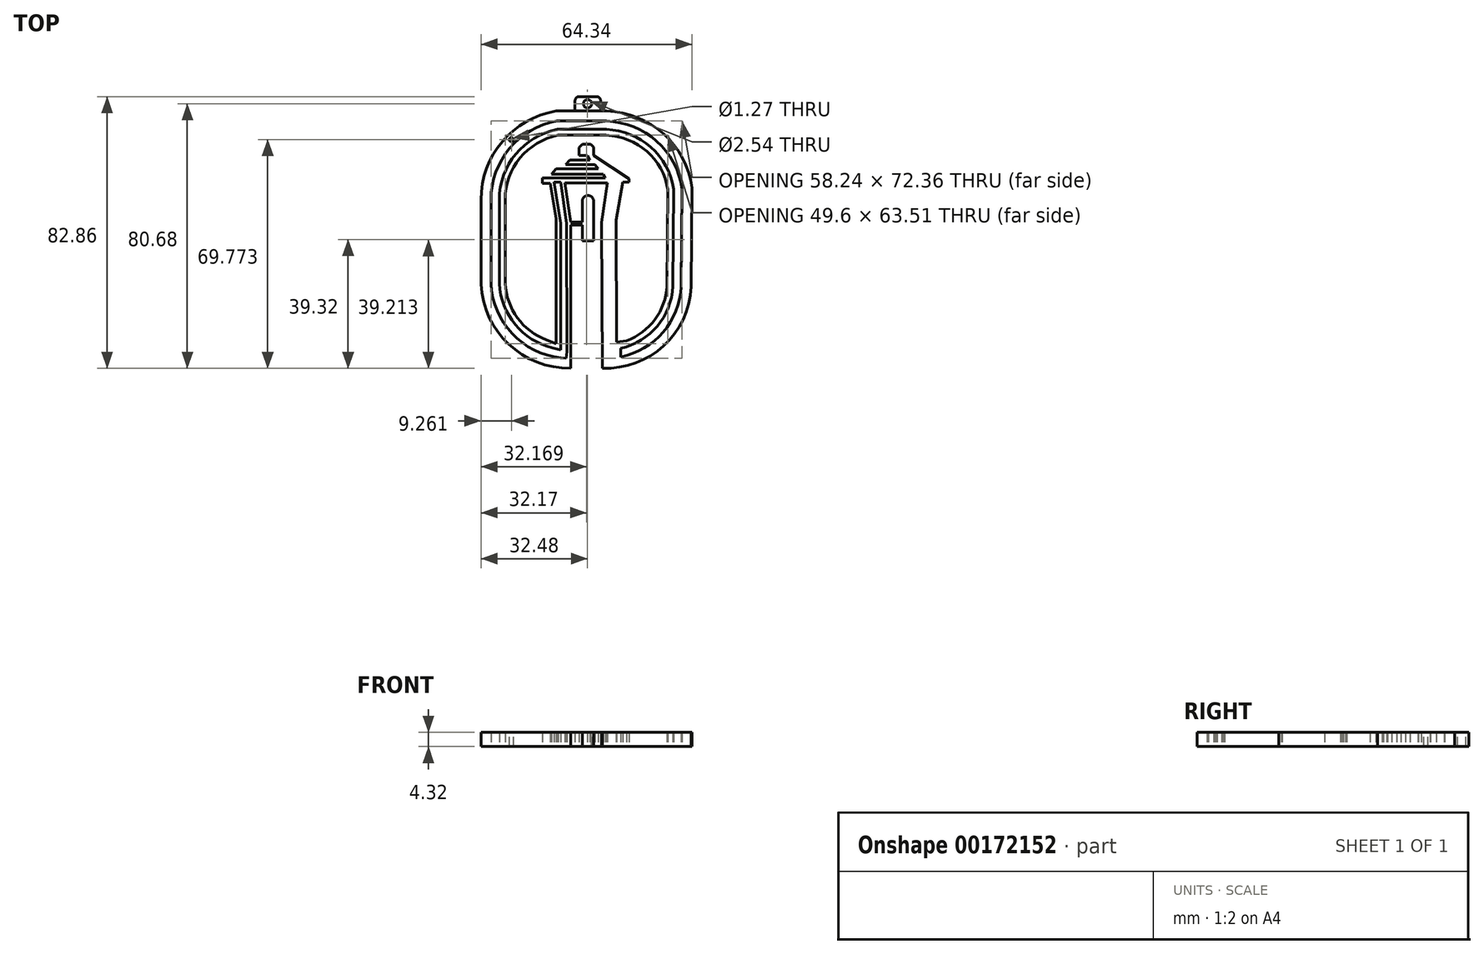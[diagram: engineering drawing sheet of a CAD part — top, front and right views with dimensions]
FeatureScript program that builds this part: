
annotation { "Feature Type Name" : "Feature", "Feature Type Description" : "" }
export const myFeature = defineFeature(function(context is Context, id is Id, definition is map)
    precondition{}
    {
        {
            var Q0;
            Q0=qCreatedBy(makeId("Top.planeOp"),FACE);
            var sketch = newSketch(context, id + "F0", { "sketchPlane" : qUnion([Q0])});
            skArc(sketch, "E0", {"start": v(-9.64, 42.68) * mm, "mid": v(-26, 33.33) * mm, "end": v(-32.48, 15.63) * mm});
            skArc(sketch, "E1", {"start": v(-32.48, -10.06) * mm, "mid": v(-24, -28.43) * mm, "end": v(-5.14, -35.74) * mm});
            skArc(sketch, "E2", {"start": v(4.52, -35.74) * mm, "mid": v(23.2, -28.91) * mm, "end": v(31.58, -10.89) * mm});
            skArc(sketch, "E3", {"start": v(31.86, 19.21) * mm, "mid": v(23.15, 35.73) * mm, "end": v(5.82, 42.68) * mm});
            skLineSegment(sketch, "E4", {"start": v(-9.64, 42.68) * mm, "end": v(5.82, 42.68) * mm});
            skLineSegment(sketch, "E5", {"start": v(-32.48, 15.63) * mm, "end": v(-32.48, -10.06) * mm});
            skLineSegment(sketch, "E6", {"start": v(31.58, -10.89) * mm, "end": v(31.86, 19.21) * mm});
            skLineSegment(sketch, "E7", {"start": v(-5.14, -35.74) * mm, "end": v(-5.14, 7.9) * mm});
            skLineSegment(sketch, "E8", {"start": v(-5.14, 8.72) * mm, "end": v(-6.88, 20.8) * mm});
            skLineSegment(sketch, "E9", {"start": v(-6.88, 20.8) * mm, "end": v(6.03, 20.8) * mm});
            skLineSegment(sketch, "E10", {"start": v(6.03, 20.8) * mm, "end": v(4.33, 8.72) * mm});
            skLineSegment(sketch, "E11", {"start": v(4.33, 8.72) * mm, "end": v(4.52, -35.74) * mm});
            skLineSegment(sketch, "E12.0", {"start": v(-9.37, 39.63) * mm, "end": v(5.78, 39.63) * mm});
            skLineSegment(sketch, "E12.1", {"start": v(-10.35, 23.5) * mm, "end": v(-10.4, 23.85) * mm});
            skLineSegment(sketch, "E12.2", {"start": v(-8.19, -30.15) * mm, "end": v(-8.19, 8.5) * mm});
            skArc(sketch, "E12.3", {"start": v(-29.43, -9.98) * mm, "mid": v(-22.96, -25.17) * mm, "end": v(-8.19, -32.55) * mm});
            skLineSegment(sketch, "E12.4", {"start": v(-29.43, 15.63) * mm, "end": v(-29.43, -9.98) * mm});
            skArc(sketch, "E12.6", {"start": v(-9.37, 39.63) * mm, "mid": v(-23.75, 31.27) * mm, "end": v(-29.43, 15.63) * mm});
            skArc(sketch, "E12.9", {"start": v(7.56, -32.63) * mm, "mid": v(22.16, -25.67) * mm, "end": v(28.54, -10.8) * mm});
            skLineSegment(sketch, "E12.10", {"start": v(28.54, -10.8) * mm, "end": v(28.8, 19.01) * mm});
            skArc(sketch, "E12.11", {"start": v(28.8, 19.01) * mm, "mid": v(21.05, 33.52) * mm, "end": v(5.78, 39.63) * mm});
            skArc(sketch, "E13.0", {"start": v(-9.14, 37.1) * mm, "mid": v(-21.88, 29.56) * mm, "end": v(-26.89, 15.63) * mm});
            skArc(sketch, "E13.4", {"start": v(-26.89, -9.92) * mm, "mid": v(-22.04, -22.38) * mm, "end": v(-10.73, -29.52) * mm});
            skLineSegment(sketch, "E13.6", {"start": v(-26.89, 15.63) * mm, "end": v(-26.89, -9.92) * mm});
            skArc(sketch, "E13.8", {"start": v(10.09, -29.68) * mm, "mid": v(21.24, -22.9) * mm, "end": v(26, -10.73) * mm});
            skLineSegment(sketch, "E13.9", {"start": v(26, -10.73) * mm, "end": v(26.27, 18.84) * mm});
            skArc(sketch, "E13.10", {"start": v(26.27, 18.84) * mm, "mid": v(19.3, 31.68) * mm, "end": v(5.74, 37.1) * mm});
            skLineSegment(sketch, "E13.11", {"start": v(-9.14, 37.1) * mm, "end": v(5.74, 37.1) * mm});
            skLineSegment(sketch, "E14.0", {"start": v(-8.97, 35.31) * mm, "end": v(5.7, 35.32) * mm});
            skArc(sketch, "E14.3", {"start": v(-25.1, -9.87) * mm, "mid": v(-21.36, -20.35) * mm, "end": v(-12.5, -27.1) * mm});
            skLineSegment(sketch, "E14.4", {"start": v(-25.1, 15.63) * mm, "end": v(-25.1, -9.87) * mm});
            skArc(sketch, "E14.6", {"start": v(-8.97, 35.31) * mm, "mid": v(-20.56, 28.36) * mm, "end": v(-25.1, 15.63) * mm});
            skArc(sketch, "E14.9", {"start": v(11.85, -27.32) * mm, "mid": v(20.56, -20.88) * mm, "end": v(24.22, -10.68) * mm});
            skLineSegment(sketch, "E14.10", {"start": v(24.22, -10.68) * mm, "end": v(24.49, 18.71) * mm});
            skArc(sketch, "E14.11", {"start": v(24.49, 18.71) * mm, "mid": v(18.08, 30.38) * mm, "end": v(5.7, 35.32) * mm});
            skLineSegment(sketch, "E15", {"start": v(1.88, 3.08) * mm, "end": v(1.88, 15.18) * mm});
            skArc(sketch, "E16", {"start": v(1.88, 15.18) * mm, "mid": v(0.12, 16.94) * mm, "end": v(-1.63, 15.18) * mm});
            skLineSegment(sketch, "E17", {"start": v(-1.63, 15.18) * mm, "end": v(-1.63, 8.8) * mm});
            skLineSegment(sketch, "E18", {"start": v(-1.63, 8.8) * mm, "end": v(-5.14, 8.8) * mm});
            skLineSegment(sketch, "E19", {"start": v(-5.14, 8.8) * mm, "end": v(-5.16, 8.84) * mm});
            skLineSegment(sketch, "E20", {"start": v(-5.14, 7.9) * mm, "end": v(-1.63, 7.9) * mm});
            skLineSegment(sketch, "E21", {"start": v(-1.63, 7.9) * mm, "end": v(-1.63, 3.08) * mm});
            skLineSegment(sketch, "E22", {"start": v(-1.63, 3.08) * mm, "end": v(1.88, 3.08) * mm});
            skLineSegment(sketch, "E23", {"start": v(-12.5, -27.1) * mm, "end": v(-9.61, -28.2) * mm});
            skLineSegment(sketch, "E24", {"start": v(-9.61, -28.2) * mm, "end": v(-9.61, 9.81) * mm});
            skLineSegment(sketch, "E25", {"start": v(-9.61, 9.81) * mm, "end": v(-11.31, 20.64) * mm});
            skLineSegment(sketch, "E26", {"start": v(-11.31, 20.64) * mm, "end": v(-13.8, 20.64) * mm});
            skLineSegment(sketch, "E27", {"start": v(-13.8, 20.64) * mm, "end": v(-13.8, 22.35) * mm});
            skLineSegment(sketch, "E28", {"start": v(-13.8, 22.35) * mm, "end": v(5.43, 22.35) * mm});
            skLineSegment(sketch, "E29", {"start": v(5.43, 22.35) * mm, "end": v(4.76, 23.5) * mm});
            skLineSegment(sketch, "E30", {"start": v(4.76, 23.5) * mm, "end": v(-11.01, 23.5) * mm});
            skLineSegment(sketch, "E31", {"start": v(-11.01, 23.5) * mm, "end": v(-9.58, 25.05) * mm});
            skLineSegment(sketch, "E32", {"start": v(-9.58, 25.05) * mm, "end": v(3.29, 25.05) * mm});
            skLineSegment(sketch, "E33", {"start": v(3.29, 25.05) * mm, "end": v(2.21, 26.4) * mm});
            skLineSegment(sketch, "E34", {"start": v(2.21, 26.4) * mm, "end": v(-6.65, 26.4) * mm});
            skLineSegment(sketch, "E35", {"start": v(-6.65, 26.4) * mm, "end": v(-5.42, 27.78) * mm});
            skLineSegment(sketch, "E36", {"start": v(-5.42, 27.78) * mm, "end": v(0.68, 27.78) * mm});
            skLineSegment(sketch, "E37", {"start": v(0.68, 27.78) * mm, "end": v(0, 29.2) * mm});
            skLineSegment(sketch, "E38", {"start": v(0, 29.2) * mm, "end": v(-2.64, 29.2) * mm});
            skLineSegment(sketch, "E39", {"start": v(-2.64, 29.2) * mm, "end": v(-2.64, 31.6) * mm});
            skLineSegment(sketch, "E40", {"start": v(-2.64, 31.6) * mm, "end": v(-1.54, 32.52) * mm});
            skLineSegment(sketch, "E41", {"start": v(-1.54, 32.52) * mm, "end": v(1, 32.52) * mm});
            skLineSegment(sketch, "E42", {"start": v(1, 32.52) * mm, "end": v(1.85, 31.66) * mm});
            skLineSegment(sketch, "E43", {"start": v(1.85, 31.66) * mm, "end": v(1.85, 29.2) * mm});
            skLineSegment(sketch, "E44", {"start": v(1.85, 29.2) * mm, "end": v(12.7, 22.05) * mm});
            skLineSegment(sketch, "E45", {"start": v(12.7, 22.05) * mm, "end": v(12.7, 20.99) * mm});
            skLineSegment(sketch, "E46", {"start": v(12.7, 20.99) * mm, "end": v(10.7, 20.99) * mm});
            skLineSegment(sketch, "E47", {"start": v(10.7, 20.99) * mm, "end": v(8.74, 9.5) * mm});
            skLineSegment(sketch, "E48", {"start": v(8.74, 9.5) * mm, "end": v(8.9, -27.8) * mm});
            skLineSegment(sketch, "E49", {"start": v(8.9, -27.8) * mm, "end": v(11.85, -27.32) * mm});
            skLineSegment(sketch, "E50", {"start": v(-10.73, -29.52) * mm, "end": v(-8.19, -30.15) * mm});
            skLineSegment(sketch, "E51", {"start": v(10.09, -29.68) * mm, "end": v(10.09, -32.27) * mm});
            skLineSegment(sketch, "E52", {"start": v(-8.19, 8.5) * mm, "end": v(-10.15, 21) * mm});
            skLineSegment(sketch, "E53", {"start": v(-10.15, 21) * mm, "end": v(-8.19, 21) * mm});
            skLineSegment(sketch, "E54", {"start": v(-8.19, 21) * mm, "end": v(-6.38, 8.5) * mm});
            skLineSegment(sketch, "E55", {"start": v(-6.38, 8.5) * mm, "end": v(-6.22, -30.63) * mm});
            skLineSegment(sketch, "E56", {"start": v(-8.19, -32.55) * mm, "end": v(-6.54, -32.73) * mm});
            skLineSegment(sketch, "E57", {"start": v(-6.54, -32.73) * mm, "end": v(-6.22, -30.63) * mm});
            skLineSegment(sketch, "E58.bottom", {"start": v(-3.8, 42.68) * mm, "end": v(4, 42.68) * mm});
            skLineSegment(sketch, "E58.top", {"start": v(-3.8, 47.1) * mm, "end": v(4, 47.1) * mm});
            skLineSegment(sketch, "E58.left", {"start": v(-3.8, 42.68) * mm, "end": v(-3.8, 47.1) * mm});
            skLineSegment(sketch, "E58.right", {"start": v(4, 42.68) * mm, "end": v(4, 47.1) * mm});
            skSolve(sketch);
        }
        {
            var Q0;
            Q0=makeQuery(id+"F0.imprint","IMPRINT",FACE,{"disambiguationData":[TD([[makeQuery(id+"F0.imprint","IMPRINT",EDGE,{"derivedFrom":sQuery(id+"F0.wireOp",EDGE,"E0")}),1.0]])]});
            var Q1;
            {var subQ4=sQuery(id+"F0.wireOp",EDGE,"E58.top");Q1=makeQuery(id+"F0.imprint","IMPRINT",FACE,{"disambiguationData":[TD([[makeQuery(id+"F0.imprint","IMPRINT",EDGE,{"derivedFrom":subQ4}),-1.0]])]});}
            extrude(context, id + "F1", {"entities" : qUnion([Q0, Q1]), "depth" : 4.32 * mm});
        }
        {
            var Q0;
            Q0=makeQuery(id+"F1.opExtrude","CAP_FACE",FACE,{"disambiguationData":[OSD([sQuery(id+"F0.wireOp",EDGE,"E0"),sQuery(id+"F0.wireOp",EDGE,"E1"),sQuery(id+"F0.wireOp",EDGE,"E2"),sQuery(id+"F0.wireOp",EDGE,"E3"),sQuery(id+"F0.wireOp",EDGE,"E4"),sQuery(id+"F0.wireOp",EDGE,"E5"),sQuery(id+"F0.wireOp",EDGE,"E6"),sQuery(id+"F0.wireOp",EDGE,"E7"),sQuery(id+"F0.wireOp",EDGE,"E8"),sQuery(id+"F0.wireOp",EDGE,"E9"),sQuery(id+"F0.wireOp",EDGE,"E10"),sQuery(id+"F0.wireOp",EDGE,"E11"),sQuery(id+"F0.wireOp",EDGE,"E12.0"),sQuery(id+"F0.wireOp",EDGE,"E12.2"),sQuery(id+"F0.wireOp",EDGE,"E12.3"),sQuery(id+"F0.wireOp",EDGE,"E12.4"),sQuery(id+"F0.wireOp",EDGE,"E12.6"),sQuery(id+"F0.wireOp",EDGE,"E12.9"),sQuery(id+"F0.wireOp",EDGE,"E12.10"),sQuery(id+"F0.wireOp",EDGE,"E12.11"),sQuery(id+"F0.wireOp",EDGE,"E13.0"),sQuery(id+"F0.wireOp",EDGE,"E13.4"),sQuery(id+"F0.wireOp",EDGE,"E13.6"),sQuery(id+"F0.wireOp",EDGE,"E13.8"),sQuery(id+"F0.wireOp",EDGE,"E13.9"),sQuery(id+"F0.wireOp",EDGE,"E13.10"),sQuery(id+"F0.wireOp",EDGE,"E13.11"),sQuery(id+"F0.wireOp",EDGE,"E14.0"),sQuery(id+"F0.wireOp",EDGE,"E14.3"),sQuery(id+"F0.wireOp",EDGE,"E14.4"),sQuery(id+"F0.wireOp",EDGE,"E14.6"),sQuery(id+"F0.wireOp",EDGE,"E14.9"),sQuery(id+"F0.wireOp",EDGE,"E14.10"),sQuery(id+"F0.wireOp",EDGE,"E14.11"),sQuery(id+"F0.wireOp",EDGE,"E15"),sQuery(id+"F0.wireOp",EDGE,"E16"),sQuery(id+"F0.wireOp",EDGE,"E17"),sQuery(id+"F0.wireOp",EDGE,"E18"),sQuery(id+"F0.wireOp",EDGE,"E19"),sQuery(id+"F0.wireOp",EDGE,"E20"),sQuery(id+"F0.wireOp",EDGE,"E21"),sQuery(id+"F0.wireOp",EDGE,"E22"),sQuery(id+"F0.wireOp",EDGE,"E23"),sQuery(id+"F0.wireOp",EDGE,"E24"),sQuery(id+"F0.wireOp",EDGE,"E25"),sQuery(id+"F0.wireOp",EDGE,"E26"),sQuery(id+"F0.wireOp",EDGE,"E27"),sQuery(id+"F0.wireOp",EDGE,"E28"),sQuery(id+"F0.wireOp",EDGE,"E29"),sQuery(id+"F0.wireOp",EDGE,"E30"),sQuery(id+"F0.wireOp",EDGE,"E31"),sQuery(id+"F0.wireOp",EDGE,"E32"),sQuery(id+"F0.wireOp",EDGE,"E33"),sQuery(id+"F0.wireOp",EDGE,"E34"),sQuery(id+"F0.wireOp",EDGE,"E35"),sQuery(id+"F0.wireOp",EDGE,"E36"),sQuery(id+"F0.wireOp",EDGE,"E37"),sQuery(id+"F0.wireOp",EDGE,"E38"),sQuery(id+"F0.wireOp",EDGE,"E39"),sQuery(id+"F0.wireOp",EDGE,"E40"),sQuery(id+"F0.wireOp",EDGE,"E41"),sQuery(id+"F0.wireOp",EDGE,"E42"),sQuery(id+"F0.wireOp",EDGE,"E43"),sQuery(id+"F0.wireOp",EDGE,"E44"),sQuery(id+"F0.wireOp",EDGE,"E45"),sQuery(id+"F0.wireOp",EDGE,"E46"),sQuery(id+"F0.wireOp",EDGE,"E47"),sQuery(id+"F0.wireOp",EDGE,"E48"),sQuery(id+"F0.wireOp",EDGE,"E49"),sQuery(id+"F0.wireOp",EDGE,"E50"),sQuery(id+"F0.wireOp",EDGE,"E51"),sQuery(id+"F0.wireOp",EDGE,"E52"),sQuery(id+"F0.wireOp",EDGE,"E53"),sQuery(id+"F0.wireOp",EDGE,"E54"),sQuery(id+"F0.wireOp",EDGE,"E55"),sQuery(id+"F0.wireOp",EDGE,"E56"),sQuery(id+"F0.wireOp",EDGE,"E57")])],"isStart":false});
            var sketch = newSketch(context, id + "F2", { "sketchPlane" : qUnion([Q0])});
            skPoint(sketch, "E59", {"position": v(-23.22, 34.01) * mm});
            skSolve(sketch);
        }
        {
            var Q0;
            Q0=sQuery(id+"F2.wireOp",VERTEX,"E59");
            var Q1;
            Q1=makeQuery(id+"F1.opExtrude","SWEPT_BODY",BODY,{"disambiguationData":[OSD([sQuery(id+"F0.wireOp",EDGE,"E0"),sQuery(id+"F0.wireOp",EDGE,"E1"),sQuery(id+"F0.wireOp",EDGE,"E2"),sQuery(id+"F0.wireOp",EDGE,"E3"),sQuery(id+"F0.wireOp",EDGE,"E4"),sQuery(id+"F0.wireOp",EDGE,"E5"),sQuery(id+"F0.wireOp",EDGE,"E6"),sQuery(id+"F0.wireOp",EDGE,"E7"),sQuery(id+"F0.wireOp",EDGE,"E8"),sQuery(id+"F0.wireOp",EDGE,"E9"),sQuery(id+"F0.wireOp",EDGE,"E10"),sQuery(id+"F0.wireOp",EDGE,"E11"),sQuery(id+"F0.wireOp",EDGE,"E12.0"),sQuery(id+"F0.wireOp",EDGE,"E12.2"),sQuery(id+"F0.wireOp",EDGE,"E12.3"),sQuery(id+"F0.wireOp",EDGE,"E12.4"),sQuery(id+"F0.wireOp",EDGE,"E12.6"),sQuery(id+"F0.wireOp",EDGE,"E12.9"),sQuery(id+"F0.wireOp",EDGE,"E12.10"),sQuery(id+"F0.wireOp",EDGE,"E12.11"),sQuery(id+"F0.wireOp",EDGE,"E13.0"),sQuery(id+"F0.wireOp",EDGE,"E13.4"),sQuery(id+"F0.wireOp",EDGE,"E13.6"),sQuery(id+"F0.wireOp",EDGE,"E13.8"),sQuery(id+"F0.wireOp",EDGE,"E13.9"),sQuery(id+"F0.wireOp",EDGE,"E13.10"),sQuery(id+"F0.wireOp",EDGE,"E13.11"),sQuery(id+"F0.wireOp",EDGE,"E14.0"),sQuery(id+"F0.wireOp",EDGE,"E14.3"),sQuery(id+"F0.wireOp",EDGE,"E14.4"),sQuery(id+"F0.wireOp",EDGE,"E14.6"),sQuery(id+"F0.wireOp",EDGE,"E14.9"),sQuery(id+"F0.wireOp",EDGE,"E14.10"),sQuery(id+"F0.wireOp",EDGE,"E14.11"),sQuery(id+"F0.wireOp",EDGE,"E15"),sQuery(id+"F0.wireOp",EDGE,"E16"),sQuery(id+"F0.wireOp",EDGE,"E17"),sQuery(id+"F0.wireOp",EDGE,"E18"),sQuery(id+"F0.wireOp",EDGE,"E19"),sQuery(id+"F0.wireOp",EDGE,"E20"),sQuery(id+"F0.wireOp",EDGE,"E21"),sQuery(id+"F0.wireOp",EDGE,"E22"),sQuery(id+"F0.wireOp",EDGE,"E23"),sQuery(id+"F0.wireOp",EDGE,"E24"),sQuery(id+"F0.wireOp",EDGE,"E25"),sQuery(id+"F0.wireOp",EDGE,"E26"),sQuery(id+"F0.wireOp",EDGE,"E27"),sQuery(id+"F0.wireOp",EDGE,"E28"),sQuery(id+"F0.wireOp",EDGE,"E29"),sQuery(id+"F0.wireOp",EDGE,"E30"),sQuery(id+"F0.wireOp",EDGE,"E31"),sQuery(id+"F0.wireOp",EDGE,"E32"),sQuery(id+"F0.wireOp",EDGE,"E33"),sQuery(id+"F0.wireOp",EDGE,"E34"),sQuery(id+"F0.wireOp",EDGE,"E35"),sQuery(id+"F0.wireOp",EDGE,"E36"),sQuery(id+"F0.wireOp",EDGE,"E37"),sQuery(id+"F0.wireOp",EDGE,"E38"),sQuery(id+"F0.wireOp",EDGE,"E39"),sQuery(id+"F0.wireOp",EDGE,"E40"),sQuery(id+"F0.wireOp",EDGE,"E41"),sQuery(id+"F0.wireOp",EDGE,"E42"),sQuery(id+"F0.wireOp",EDGE,"E43"),sQuery(id+"F0.wireOp",EDGE,"E44"),sQuery(id+"F0.wireOp",EDGE,"E45"),sQuery(id+"F0.wireOp",EDGE,"E46"),sQuery(id+"F0.wireOp",EDGE,"E47"),sQuery(id+"F0.wireOp",EDGE,"E48"),sQuery(id+"F0.wireOp",EDGE,"E49"),sQuery(id+"F0.wireOp",EDGE,"E50"),sQuery(id+"F0.wireOp",EDGE,"E51"),sQuery(id+"F0.wireOp",EDGE,"E52"),sQuery(id+"F0.wireOp",EDGE,"E53"),sQuery(id+"F0.wireOp",EDGE,"E54"),sQuery(id+"F0.wireOp",EDGE,"E55"),sQuery(id+"F0.wireOp",EDGE,"E56"),sQuery(id+"F0.wireOp",EDGE,"E57")])]});
            hole(context, id + "F3", {"style" : HoleStyle.SIMPLE, "endStyle" : HoleEndStyle.THROUGH, "holeDiameter" : 1.27 * mm, "locations" : qUnion([Q0]), "scope" : qUnion([Q1]), "isTappedThrough" : true});
        }
        {
            var Q0;
            Q0=makeQuery(id+"F1.opExtrude","SWEPT_EDGE",EDGE,{"disambiguationData":[OSD([sQuery(id+"F0.wireOp",EDGE,"E58.top"),sQuery(id+"F0.wireOp",EDGE,"E58.left")])]});
            var Q1;
            Q1=makeQuery(id+"F1.opExtrude","SWEPT_EDGE",EDGE,{"disambiguationData":[OSD([sQuery(id+"F0.wireOp",EDGE,"E58.top"),sQuery(id+"F0.wireOp",EDGE,"E58.right")])]});
            fillet(context, id + "F4", {"entities" : qUnion([Q0, Q1]), "radius" : 1.27 * mm, "tangentPropagation" : true, "allowEdgeOverflow" : false});
        }
        {
            var Q0;
            Q0=makeQuery(id+"F1.opExtrude","CAP_FACE",FACE,{"disambiguationData":[OSD([sQuery(id+"F0.wireOp",EDGE,"E4"),sQuery(id+"F0.wireOp",EDGE,"E58.top"),sQuery(id+"F0.wireOp",EDGE,"E58.left"),sQuery(id+"F0.wireOp",EDGE,"E58.right")])],"isStart":false});
            var sketch = newSketch(context, id + "F5", { "sketchPlane" : qUnion([Q0])});
            skPoint(sketch, "E60", {"position": v(0, 44.92) * mm});
            skSolve(sketch);
        }
        {
            var Q0;
            Q0=sQuery(id+"F5.wireOp",VERTEX,"E60");
            var Q1;
            Q1=makeQuery(id+"F1.opExtrude","SWEPT_BODY",BODY,{"disambiguationData":[OSD([sQuery(id+"F0.wireOp",EDGE,"E4"),sQuery(id+"F0.wireOp",EDGE,"E58.top"),sQuery(id+"F0.wireOp",EDGE,"E58.left"),sQuery(id+"F0.wireOp",EDGE,"E58.right")])]});
            hole(context, id + "F6", {"style" : HoleStyle.SIMPLE, "endStyle" : HoleEndStyle.THROUGH, "holeDiameter" : 2.54 * mm, "isTappedThrough" : true, "tappedDepth" : 12.7 * mm, "tapClearance" : 3, "locations" : qUnion([Q0]), "scope" : qUnion([Q1])});
        }
    });
